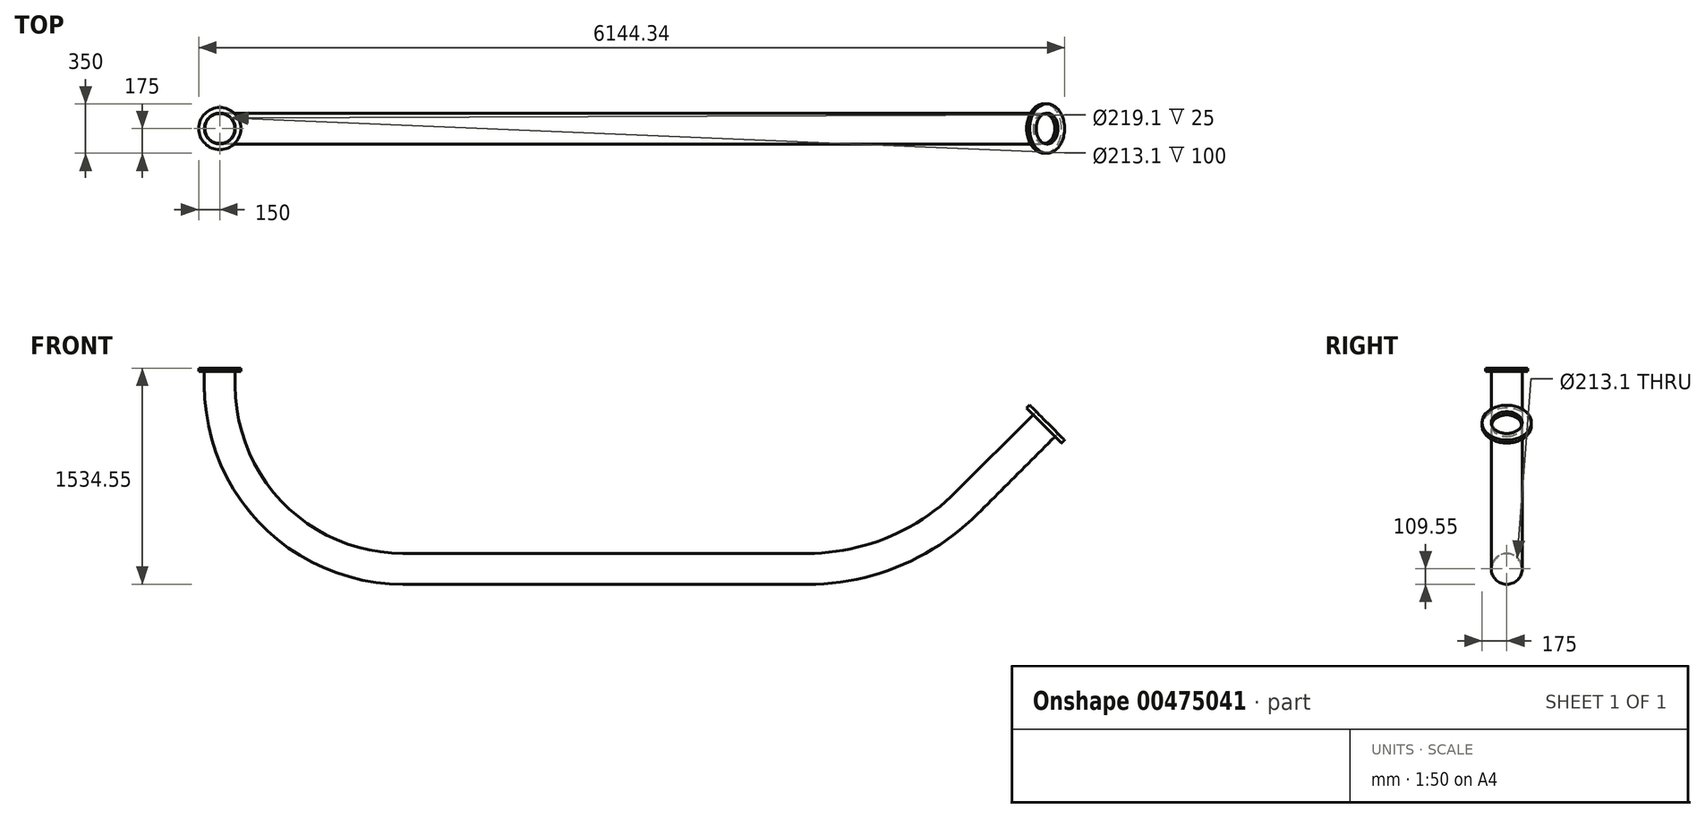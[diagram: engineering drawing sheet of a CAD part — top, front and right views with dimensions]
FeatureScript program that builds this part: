
annotation { "Feature Type Name" : "Feature", "Feature Type Description" : "" }
export const myFeature = defineFeature(function(context is Context, id is Id, definition is map)
    precondition{}
    {
        {
            var Q0;
            Q0=qCreatedBy(makeId("Front.planeOp"),FACE);
            var sketch = newSketch(context, id + "F0", { "sketchPlane" : qUnion([Q0])});
            skLineSegment(sketch, "E0", {"start": v(-1435, 0) * mm, "end": v(1435, 0) * mm, "construction": true});
            skArc(sketch, "E1", {"start": v(-1435, 0) * mm, "mid": v(-2354.24, 380.76) * mm, "end": v(-2735, 1300) * mm, "construction": true});
            skPoint(sketch, "E2", {"position": v(0, 0) * mm});
            skArc(sketch, "E3.5", {"start": v(-1435, -109.55) * mm, "mid": v(-2431.7, 303.3) * mm, "end": v(-2844.55, 1300) * mm});
            skLineSegment(sketch, "E3.6", {"start": v(-1435, -109.55) * mm, "end": v(1435, -109.55) * mm});
            skLineSegment(sketch, "E4", {"start": v(-1435, 0) * mm, "end": v(-1435, -109.55) * mm});
            skLineSegment(sketch, "E5", {"start": v(-2844.55, 1300) * mm, "end": v(-2735, 1300) * mm});
            skLineSegment(sketch, "E6", {"start": v(0, 0) * mm, "end": v(0, -109.55) * mm, "construction": true});
            skLineSegment(sketch, "E7.MirrorCS", {"start": v(1435, 0) * mm, "end": v(1435, -109.55) * mm});
            skLineSegment(sketch, "E8", {"start": v(-2735, 1300) * mm, "end": v(-2735, 1400) * mm, "construction": true});
            skLineSegment(sketch, "E9", {"start": v(-2735, 1400) * mm, "end": v(-2844.55, 1400) * mm});
            skLineSegment(sketch, "E10", {"start": v(-2844.55, 1400) * mm, "end": v(-2844.55, 1300) * mm});
            skLineSegment(sketch, "E11.bottom", {"start": v(2677.6, -159.55) * mm, "end": v(-2522.4, -159.55) * mm, "construction": true});
            skLineSegment(sketch, "E11.top", {"start": v(3077.6, 540.45) * mm, "end": v(-2922.4, 540.45) * mm, "construction": true});
            skLineSegment(sketch, "E11.left", {"start": v(3077.6, 340.45) * mm, "end": v(3077.6, 540.45) * mm, "construction": true});
            skLineSegment(sketch, "E11.right", {"start": v(-2922.4, 340.45) * mm, "end": v(-2922.4, 540.45) * mm, "construction": true});
            skLineSegment(sketch, "E12", {"start": v(-2922.4, 340.45) * mm, "end": v(-2522.4, -159.55) * mm, "construction": true});
            skLineSegment(sketch, "E13", {"start": v(2677.6, -159.55) * mm, "end": v(3077.6, 340.45) * mm, "construction": true});
            skPoint(sketch, "E14", {"position": v(0, -159.55) * mm});
            skLineSegment(sketch, "E15", {"start": v(-2622.4, 540.45) * mm, "end": v(-2622.4, -34.55) * mm, "construction": true});
            skLineSegment(sketch, "E16", {"start": v(-2622.4, 540.45) * mm, "end": v(-2222.4, 40.45) * mm});
            skArc(sketch, "E17", {"start": v(1435, 0) * mm, "mid": v(2047.3, 121.8) * mm, "end": v(2566.37, 468.63) * mm, "construction": true});
            skArc(sketch, "E18", {"start": v(1435, -109.55) * mm, "mid": v(2089.22, 20.58) * mm, "end": v(2643.83, 391.17) * mm});
            skLineSegment(sketch, "E19", {"start": v(2566.37, 468.63) * mm, "end": v(2643.83, 391.17) * mm});
            skLineSegment(sketch, "E20", {"start": v(2643.83, 391.17) * mm, "end": v(3191.84, 939.17) * mm});
            skLineSegment(sketch, "E21", {"start": v(3191.84, 939.17) * mm, "end": v(3114.38, 1016.64) * mm});
            skLineSegment(sketch, "E22", {"start": v(3114.38, 1016.64) * mm, "end": v(2566.37, 468.63) * mm, "construction": true});
            skLineSegment(sketch, "E23", {"start": v(2776.6, 540.45) * mm, "end": v(2216.6, -159.55) * mm, "construction": true});
            skSolve(sketch);
        }
        {
            var Q0;
            Q0=qCreatedBy(makeId("Front.planeOp"),FACE);
            var sketch = newSketch(context, id + "F1", { "sketchPlane" : qUnion([Q0])});
            skLineSegment(sketch, "E24", {"start": v(-2841.55, 1400) * mm, "end": v(-2841.55, 1300) * mm});
            skLineSegment(sketch, "E25", {"start": v(-2844.55, 1400) * mm, "end": v(-2841.55, 1400) * mm});
            skLineSegment(sketch, "E26", {"start": v(-2844.55, 1300) * mm, "end": v(-2841.55, 1300) * mm});
            skLineSegment(sketch, "E27", {"start": v(-2844.55, 1300) * mm, "end": v(-2844.55, 1400) * mm});
            skSolve(sketch);
        }
        {
            var Q0;
            Q0=makeQuery(id+"F1.imprint","IMPRINT",FACE,{"disambiguationData":[TD([[makeQuery(id+"F1.imprint","IMPRINT",EDGE,{"derivedFrom":sQuery(id+"F1.wireOp",EDGE,"E24")}),-1.0]])]});
            var Q1;
            Q1=sQuery(id+"F0.wireOp",EDGE,"E8");
            revolve(context, id + "F2", {"entities" : qUnion([Q0]), "axis" : qUnion([Q1]), "revolveType" : RevolveType.FULL});
        }
        {
            var Q0;
            Q0=makeQuery(id+"F2.opRevolve","SWEPT_FACE",FACE,{"disambiguationData":[OSD([sQuery(id+"F1.wireOp",EDGE,"E26")])]});
            var Q1;
            Q1=sQuery(id+"F0.wireOp",EDGE,"E3.3");
            var Q2;
            Q2=sQuery(id+"F0.wireOp",EDGE,"ehUSYPVM-8In4-UokY-o1ir-dxswM0NRwGns");
            var Q3;
            Q3=sQuery(id+"F0.wireOp",EDGE,"E3.5");
            var Q4;
            Q4=sQuery(id+"F0.wireOp",EDGE,"E3.6");
            var Q5;
            Q5=sQuery(id+"F0.wireOp",EDGE,"d5dcd199-87a5-43e9-9218-31ebdbec5ac011.MirrorCS");
            var Q6;
            Q6=sQuery(id+"F0.wireOp",EDGE,"d5dcd199-87a5-43e9-9218-31ebdbec5ac07.MirrorCS");
            var Q7;
            Q7=sQuery(id+"F0.wireOp",EDGE,"d5dcd199-87a5-43e9-9218-31ebdbec5ac03.MirrorCS");
            var Q8;
            Q8=sQuery(id+"F0.wireOp",EDGE,"d5dcd199-87a5-43e9-9218-31ebdbec5ac09.MirrorCS");
            var Q9;
            Q9=sQuery(id+"F0.wireOp",EDGE,"913ca05b-7b36-42bc-a168-2c98df43f88b0.MirrorCS");
            sweep(context, id + "F3", {"operationType" : NewBodyOperationType.ADD, "profiles" : qUnion([Q0]), "path" : qUnion([Q1, Q2, Q3, Q4, Q5, Q6, Q7, Q8, Q9])});
        }
        {
            var Q0;
            Q0=makeQuery(id+"F3.opSweep","CAP_FACE",FACE,{"disambiguationData":[OSD([sQuery(id+"F0.wireOp",VERTEX,"E3.6.end"),dummyQuery(id+"FcjeWj101vwSLZw_0.vertexPlane.planeOp",FACE)])],"isStart":false});
            var Q1;
            Q1=sQuery(id+"F0.wireOp",EDGE,"E18");
            var Q2;
            Q2=sQuery(id+"F0.wireOp",EDGE,"E20");
            sweep(context, id + "F4", {"operationType" : NewBodyOperationType.ADD, "profiles" : qUnion([Q0]), "path" : qUnion([Q1, Q2])});
        }
        {
            var Q0;
            Q0=makeQuery(id+"F2.opRevolve","SWEPT_FACE",FACE,{"disambiguationData":[OSD([sQuery(id+"F1.wireOp",EDGE,"E25")])]});
            var sketch = newSketch(context, id + "F5", { "sketchPlane" : qUnion([Q0])});
            skCircle(sketch, "E28", {"center": v(-2735, 0) * mm, "radius": 150 * mm});
            skCircle(sketch, "E29", {"center": v(-2735, 0) * mm, "radius": 109.55 * mm});
            skSolve(sketch);
        }
        {
            var Q0;
            Q0=makeQuery(id+"F5.imprint","IMPRINT",FACE,{"disambiguationData":[TD([[makeQuery(id+"F5.imprint","IMPRINT",EDGE,{"derivedFrom":sQuery(id+"F5.wireOp",EDGE,"E28")}),1.0]])]});
            var Q1;
            Q1=makeQuery(id+"F5.imprint","IMPRINT",FACE,{"disambiguationData":[TD([[makeQuery(id+"F5.imprint","IMPRINT",EDGE,{"derivedFrom":sQuery(id+"F5.wireOp",EDGE,"y8ymGNpF-K1WR-XcHZ-xaFE-vk0SO8xZg14S")}),1.0]])]});
            var Q2;
            Q2=sQuery(id+"F5.wireOp",EDGE,"E28");
            extrude(context, id + "F6", {"entities" : qUnion([Q0, Q1]), "surfaceEntities" : qUnion([Q2]), "depth" : 25 * mm});
        }
        {
            var Q0;
            Q0=makeQuery(id+"F4.opSweep","CAP_FACE",FACE,{"disambiguationData":[OSD([sQuery(id+"F0.wireOp",VERTEX,"E3.6.end"),sQuery(id+"F0.wireOp",VERTEX,"E20.end"),dummyQuery(id+"FcjeWj101vwSLZw_0.vertexPlane.planeOp",FACE)])],"isStart":false});
            var sketch = newSketch(context, id + "F7", { "sketchPlane" : qUnion([Q0])});
            skCircle(sketch, "E30", {"center": v(0, -1483.33) * mm, "radius": 175 * mm});
            skCircle(sketch, "E31", {"center": v(0, -1483.33) * mm, "radius": 106.55 * mm});
            skSolve(sketch);
        }
        {
            var Q0;
            Q0=makeQuery(id+"F7.imprint","IMPRINT",FACE,{"disambiguationData":[TD([[makeQuery(id+"F7.imprint","IMPRINT",EDGE,{"derivedFrom":sQuery(id+"F7.wireOp",EDGE,"E30")}),1.0]])]});
            extrude(context, id + "F8", {"entities" : qUnion([Q0]), "depth" : 30 * mm});
        }
    });
